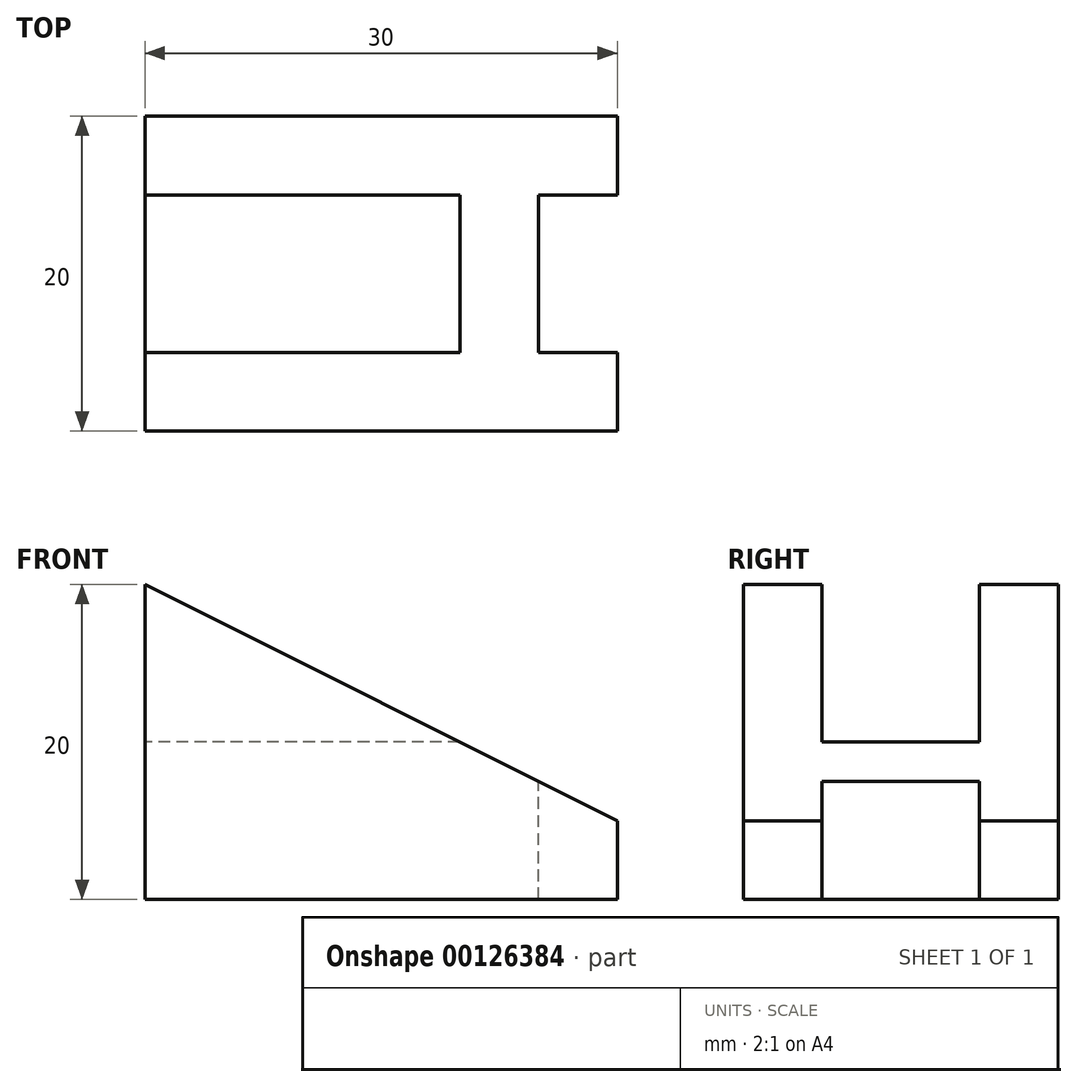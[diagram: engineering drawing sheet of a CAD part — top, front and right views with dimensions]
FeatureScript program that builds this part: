
annotation { "Feature Type Name" : "Feature", "Feature Type Description" : "" }
export const myFeature = defineFeature(function(context is Context, id is Id, definition is map)
    precondition{}
    {
        {
            var Q0;
            Q0=qCreatedBy(makeId("Front.planeOp"),FACE);
            var sketch = newSketch(context, id + "F0", { "sketchPlane" : qUnion([Q0])});
            skLineSegment(sketch, "E0", {"start": v(0, 20) * mm, "end": v(0, 0) * mm});
            skLineSegment(sketch, "E1", {"start": v(0, 0) * mm, "end": v(30, 0) * mm});
            skLineSegment(sketch, "E2", {"start": v(30, 0) * mm, "end": v(30, 5) * mm});
            skLineSegment(sketch, "E3", {"start": v(30, 5) * mm, "end": v(0, 20) * mm});
            skSolve(sketch);
        }
        {
            var Q0;
            Q0 = qSketchRegion(id + "F0", true);
            extrude(context, id + "F1", {"entities" : qUnion([Q0]), "depth" : 20 * mm});
        }
        {
            var Q0;
            Q0=makeQuery(id+"F1.opExtrude","SWEPT_FACE",FACE,{"disambiguationData":[OSD([sQuery(id+"F0.wireOp",EDGE,"E2")])]});
            var sketch = newSketch(context, id + "F2", { "sketchPlane" : qUnion([Q0])});
            skLineSegment(sketch, "E4.bottom", {"start": v(-15, 0) * mm, "end": v(-5, 0) * mm});
            skLineSegment(sketch, "E4.top", {"start": v(-15, 7.5) * mm, "end": v(-5, 7.5) * mm});
            skLineSegment(sketch, "E4.left", {"start": v(-15, 0) * mm, "end": v(-15, 7.5) * mm});
            skLineSegment(sketch, "E4.right", {"start": v(-5, 0) * mm, "end": v(-5, 7.5) * mm});
            skSolve(sketch);
        }
        {
            var Q0;
            Q0 = qSketchRegion(id + "F2", true);
            extrude(context, id + "F3", {"entities" : qUnion([Q0]), "operationType" : NewBodyOperationType.REMOVE, "oppositeDirection" : true, "depth" : 5 * mm});
        }
        {
            var Q0;
            Q0=makeQuery(id+"F1.opExtrude","SWEPT_FACE",FACE,{"disambiguationData":[OSD([sQuery(id+"F0.wireOp",EDGE,"E0")])]});
            var sketch = newSketch(context, id + "F4", { "sketchPlane" : qUnion([Q0])});
            skLineSegment(sketch, "E5.bottom", {"start": v(5, 20) * mm, "end": v(15, 20) * mm});
            skLineSegment(sketch, "E5.top", {"start": v(5, 10) * mm, "end": v(15, 10) * mm});
            skLineSegment(sketch, "E5.left", {"start": v(5, 20) * mm, "end": v(5, 10) * mm});
            skLineSegment(sketch, "E5.right", {"start": v(15, 20) * mm, "end": v(15, 10) * mm});
            skSolve(sketch);
        }
        {
            var Q0;
            Q0 = qSketchRegion(id + "F4", true);
            extrude(context, id + "F5", {"entities" : qUnion([Q0]), "operationType" : NewBodyOperationType.REMOVE, "oppositeDirection" : true, "depth" : 20 * mm});
        }
    });
